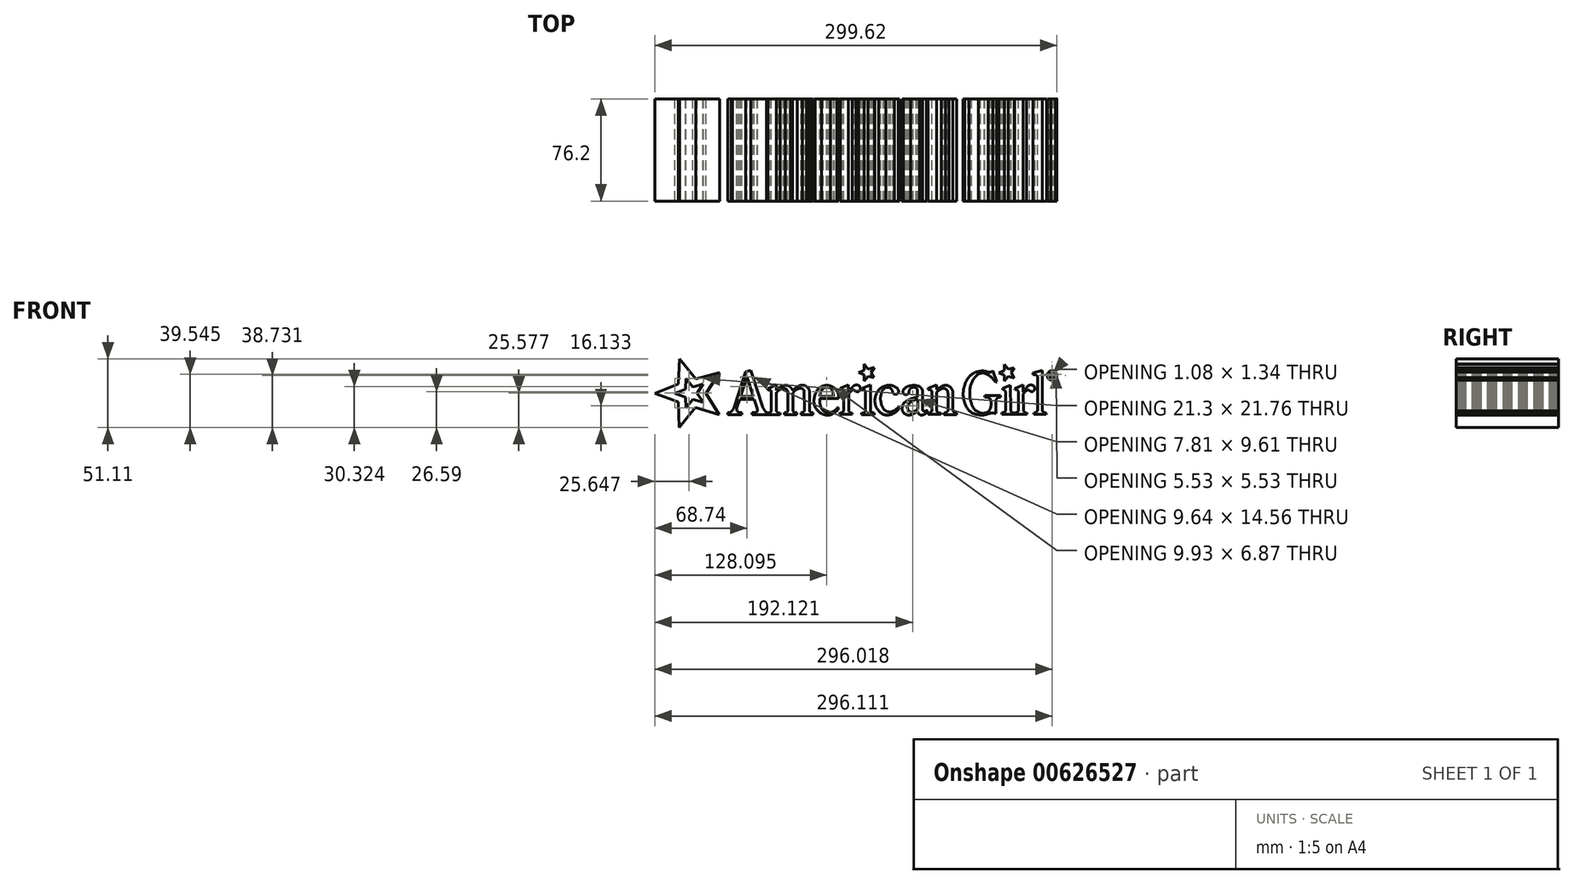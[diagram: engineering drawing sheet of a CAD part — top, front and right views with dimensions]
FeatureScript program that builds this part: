
annotation { "Feature Type Name" : "Feature", "Feature Type Description" : "" }
export const myFeature = defineFeature(function(context is Context, id is Id, definition is map)
    precondition{}
    {
        {
            var Q0;
            Q0=qCreatedBy(makeId("Front.planeOp"),FACE);
            var sketch = newSketch(context, id + "F0", { "sketchPlane" : qUnion([Q0])});
            skLineSegment(sketch, "E0", {"start": v(-64.16, 36.86) * mm, "end": v(-72.1, 33.85) * mm});
            skLineSegment(sketch, "E1", {"start": v(-72.1, 33.85) * mm, "end": v(-64.16, 31.03) * mm});
            skLineSegment(sketch, "E2", {"start": v(-64.16, 31.03) * mm, "end": v(-63.64, 23.1) * mm});
            skLineSegment(sketch, "E3", {"start": v(-63.64, 23.1) * mm, "end": v(-58.72, 29.32) * mm});
            skLineSegment(sketch, "E4", {"start": v(-58.72, 29.32) * mm, "end": v(-50.8, 26.96) * mm});
            skLineSegment(sketch, "E5", {"start": v(-50.8, 26.96) * mm, "end": v(-55.38, 33.85) * mm});
            skLineSegment(sketch, "E6", {"start": v(-55.38, 33.85) * mm, "end": v(-50.92, 40.6) * mm});
            skLineSegment(sketch, "E7", {"start": v(-50.92, 40.6) * mm, "end": v(-58.6, 38.5) * mm});
            skLineSegment(sketch, "E8", {"start": v(-58.6, 38.5) * mm, "end": v(-63.64, 44.86) * mm});
            skLineSegment(sketch, "E9", {"start": v(-63.64, 44.86) * mm, "end": v(-64.16, 36.86) * mm});
            skLineSegment(sketch, "E10", {"start": v(-69.43, 40.6) * mm, "end": v(-87.1, 33.85) * mm});
            skPoint(sketch, "E10.endSnap0", {"position": v(-87.1, 33.95) * mm});
            skLineSegment(sketch, "E11", {"start": v(-87.1, 33.85) * mm, "end": v(-69.33, 27.53) * mm});
            skLineSegment(sketch, "E12", {"start": v(-69.33, 27.53) * mm, "end": v(-68.79, 8.4) * mm});
            skLineSegment(sketch, "E13", {"start": v(-68.79, 8.4) * mm, "end": v(-56.93, 23.25) * mm});
            skLineSegment(sketch, "E14", {"start": v(-56.93, 23.25) * mm, "end": v(-38.87, 17.96) * mm});
            skLineSegment(sketch, "E15", {"start": v(-38.87, 17.96) * mm, "end": v(-48.84, 33.79) * mm});
            skLineSegment(sketch, "E16", {"start": v(-48.84, 33.79) * mm, "end": v(-38.56, 49.4) * mm});
            skLineSegment(sketch, "E17", {"start": v(-38.56, 49.4) * mm, "end": v(-56.57, 44.63) * mm});
            skLineSegment(sketch, "E18", {"start": v(-56.57, 44.63) * mm, "end": v(-68.38, 59.5) * mm});
            skLineSegment(sketch, "E19", {"start": v(-68.38, 59.5) * mm, "end": v(-69.43, 40.6) * mm});
            skLineSegment(sketch, "E20", {"start": v(-23.17, 31.44) * mm, "end": v(-13.53, 31.44) * mm});
            skLineSegment(sketch, "E21", {"start": v(-13.53, 31.44) * mm, "end": v(-18.27, 46) * mm});
            skLineSegment(sketch, "E22", {"start": v(-18.27, 46) * mm, "end": v(-23.17, 31.44) * mm});
            skLineSegment(sketch, "E23", {"start": v(-19.42, 49.88) * mm, "end": v(-15.52, 50.95) * mm});
            skLineSegment(sketch, "E24", {"start": v(-23.84, 29.47) * mm, "end": v(-13.1, 29.47) * mm});
            skLineSegment(sketch, "E25", {"start": v(-15.52, 50.95) * mm, "end": v(-6.5, 23.57) * mm});
            skLineSegment(sketch, "E26", {"start": v(-19.42, 49.88) * mm, "end": v(-28.04, 23.24) * mm});
            skLineSegment(sketch, "E27", {"start": v(-23.84, 29.47) * mm, "end": v(-25.84, 22.87) * mm});
            skLineSegment(sketch, "E28", {"start": v(-13.1, 29.47) * mm, "end": v(-10.8, 22.62) * mm});
            skLineSegment(sketch, "E29", {"start": v(-32.76, 19.4) * mm, "end": v(-32.76, 18.03) * mm});
            skLineSegment(sketch, "E30", {"start": v(-32.76, 18.03) * mm, "end": v(-22.12, 18.03) * mm});
            skLineSegment(sketch, "E31", {"start": v(-22.12, 18.03) * mm, "end": v(-22.12, 19.34) * mm});
            skLineSegment(sketch, "E32", {"start": v(-22.12, 19.34) * mm, "end": v(-23.42, 19.34) * mm});
            skLineSegment(sketch, "E33", {"start": v(-32.76, 19.4) * mm, "end": v(-31.77, 19.4) * mm});
            skLineSegment(sketch, "E34", {"start": v(-14.62, 19.43) * mm, "end": v(-14.62, 18) * mm});
            skLineSegment(sketch, "E35", {"start": v(-14.62, 18) * mm, "end": v(6.53, 18) * mm});
            skLineSegment(sketch, "E36", {"start": v(6.53, 18) * mm, "end": v(6.53, 19.13) * mm});
            skLineSegment(sketch, "E37", {"start": v(6.53, 19.13) * mm, "end": v(5.77, 19.13) * mm});
            skLineSegment(sketch, "E38", {"start": v(-14.62, 19.43) * mm, "end": v(-12.2, 19.43) * mm});
            skArc(sketch, "E39", {"start": v(-12.2, 19.43) * mm, "mid": v(-11.19, 19.79) * mm, "end": v(-10.62, 20.7) * mm});
            skArc(sketch, "E40", {"start": v(-10.62, 20.7) * mm, "mid": v(-10.56, 21.23) * mm, "end": v(-10.62, 21.77) * mm});
            skArc(sketch, "E41", {"start": v(-10.62, 21.77) * mm, "mid": v(-10.7, 22.2) * mm, "end": v(-10.8, 22.62) * mm});
            skArc(sketch, "E42", {"start": v(-24.65, 19.83) * mm, "mid": v(-24.08, 19.47) * mm, "end": v(-23.42, 19.34) * mm});
            skArc(sketch, "E43", {"start": v(-25.68, 20.8) * mm, "mid": v(-25.28, 20.2) * mm, "end": v(-24.65, 19.83) * mm});
            skArc(sketch, "E44", {"start": v(-25.84, 22.87) * mm, "mid": v(-25.95, 21.82) * mm, "end": v(-25.68, 20.8) * mm});
            skArc(sketch, "E45", {"start": v(-31.77, 19.4) * mm, "mid": v(-30.94, 19.57) * mm, "end": v(-30.27, 20.09) * mm});
            skArc(sketch, "E46", {"start": v(-30.27, 20.09) * mm, "mid": v(-29.58, 20.62) * mm, "end": v(-29.03, 21.3) * mm});
            skArc(sketch, "E47", {"start": v(-29.03, 21.3) * mm, "mid": v(-28.45, 22.23) * mm, "end": v(-28.04, 23.24) * mm});
            skArc(sketch, "E48", {"start": v(-6.5, 23.57) * mm, "mid": v(-5.45, 21.42) * mm, "end": v(-3.88, 19.62) * mm});
            skArc(sketch, "E49", {"start": v(-3.88, 19.62) * mm, "mid": v(-2.4, 19.27) * mm, "end": v(-0.93, 19.62) * mm});
            skArc(sketch, "E50", {"start": v(-0.93, 19.62) * mm, "mid": v(-0.43, 20.28) * mm, "end": v(-0.25, 21.07) * mm});
            skLineSegment(sketch, "E51", {"start": v(-0.25, 21.07) * mm, "end": v(-0.25, 34.6) * mm});
            skArc(sketch, "E52", {"start": v(-0.25, 34.6) * mm, "mid": v(-0.32, 35.18) * mm, "end": v(-0.5, 35.73) * mm});
            skArc(sketch, "E53", {"start": v(-0.5, 35.73) * mm, "mid": v(-0.88, 36.15) * mm, "end": v(-1.41, 36.3) * mm});
            skArc(sketch, "E54", {"start": v(-1.41, 36.3) * mm, "mid": v(-2.1, 36.39) * mm, "end": v(-2.78, 36.3) * mm});
            skLineSegment(sketch, "E55", {"start": v(-2.78, 36.3) * mm, "end": v(-2.78, 37.36) * mm});
            skLineSegment(sketch, "E56", {"start": v(-2.78, 37.36) * mm, "end": v(3.53, 40.06) * mm});
            skLineSegment(sketch, "E57", {"start": v(3.53, 40.06) * mm, "end": v(3.53, 35.88) * mm});
            skArc(sketch, "E58", {"start": v(3.78, 20.36) * mm, "mid": v(4.6, 19.46) * mm, "end": v(5.77, 19.13) * mm});
            skArc(sketch, "E59", {"start": v(3.57, 21.04) * mm, "mid": v(3.63, 20.68) * mm, "end": v(3.78, 20.36) * mm});
            skLineSegment(sketch, "E60", {"start": v(3.57, 21.04) * mm, "end": v(3.57, 34.16) * mm});
            skArc(sketch, "E61", {"start": v(4.9, 35.53) * mm, "mid": v(4.18, 34.9) * mm, "end": v(3.57, 34.16) * mm});
            skArc(sketch, "E62", {"start": v(8.49, 37.37) * mm, "mid": v(6.53, 36.77) * mm, "end": v(4.9, 35.53) * mm});
            skArc(sketch, "E63", {"start": v(10.72, 37.05) * mm, "mid": v(9.63, 37.39) * mm, "end": v(8.49, 37.37) * mm});
            skArc(sketch, "E64", {"start": v(12.05, 34.48) * mm, "mid": v(11.7, 35.93) * mm, "end": v(10.72, 37.05) * mm});
            skLineSegment(sketch, "E65", {"start": v(12.05, 34.48) * mm, "end": v(12.05, 21.12) * mm});
            skArc(sketch, "E66", {"start": v(11.67, 19.95) * mm, "mid": v(11.95, 20.5) * mm, "end": v(12.05, 21.12) * mm});
            skArc(sketch, "E67", {"start": v(9.45, 19.36) * mm, "mid": v(10.61, 19.44) * mm, "end": v(11.67, 19.95) * mm});
            skLineSegment(sketch, "E68", {"start": v(9.45, 19.36) * mm, "end": v(9.45, 17.88) * mm});
            skLineSegment(sketch, "E69", {"start": v(9.45, 17.88) * mm, "end": v(18.73, 17.88) * mm});
            skLineSegment(sketch, "E70", {"start": v(18.73, 17.88) * mm, "end": v(18.73, 19.36) * mm});
            skLineSegment(sketch, "E71", {"start": v(15.84, 34.27) * mm, "end": v(15.84, 21.13) * mm});
            skArc(sketch, "E72", {"start": v(15.84, 21.13) * mm, "mid": v(16.92, 19.65) * mm, "end": v(18.73, 19.36) * mm});
            skArc(sketch, "E73", {"start": v(19.18, 36.87) * mm, "mid": v(17.39, 35.72) * mm, "end": v(15.84, 34.27) * mm});
            skArc(sketch, "E74", {"start": v(22.82, 37.28) * mm, "mid": v(20.96, 37.47) * mm, "end": v(19.18, 36.87) * mm});
            skArc(sketch, "E75", {"start": v(24.33, 34.88) * mm, "mid": v(23.94, 36.3) * mm, "end": v(22.82, 37.28) * mm});
            skLineSegment(sketch, "E76", {"start": v(24.33, 34.88) * mm, "end": v(24.48, 21.7) * mm});
            skArc(sketch, "E77", {"start": v(23.86, 19.84) * mm, "mid": v(24.33, 20.72) * mm, "end": v(24.48, 21.7) * mm});
            skArc(sketch, "E78", {"start": v(21.8, 19.34) * mm, "mid": v(22.86, 19.46) * mm, "end": v(23.86, 19.84) * mm});
            skLineSegment(sketch, "E79", {"start": v(21.8, 19.34) * mm, "end": v(21.8, 17.93) * mm});
            skLineSegment(sketch, "E80", {"start": v(21.8, 17.93) * mm, "end": v(31, 17.93) * mm});
            skLineSegment(sketch, "E81", {"start": v(31, 17.93) * mm, "end": v(31, 19.34) * mm});
            skArc(sketch, "E82", {"start": v(28.79, 19.88) * mm, "mid": v(29.85, 19.44) * mm, "end": v(31, 19.34) * mm});
            skArc(sketch, "E83", {"start": v(28.39, 20.94) * mm, "mid": v(28.46, 20.36) * mm, "end": v(28.79, 19.88) * mm});
            skLineSegment(sketch, "E84", {"start": v(28.39, 20.94) * mm, "end": v(28.39, 34.4) * mm});
            skArc(sketch, "E85", {"start": v(28.39, 34.4) * mm, "mid": v(27.77, 36.88) * mm, "end": v(26.06, 38.78) * mm});
            skArc(sketch, "E86", {"start": v(26.06, 38.78) * mm, "mid": v(24.61, 39.6) * mm, "end": v(22.94, 39.68) * mm});
            skArc(sketch, "E87", {"start": v(22.94, 39.68) * mm, "mid": v(20.9, 39.5) * mm, "end": v(19.09, 38.6) * mm});
            skArc(sketch, "E88", {"start": v(19.09, 38.6) * mm, "mid": v(17.27, 37.37) * mm, "end": v(15.68, 35.85) * mm});
            skArc(sketch, "E89", {"start": v(15.68, 35.85) * mm, "mid": v(15.03, 37.25) * mm, "end": v(13.96, 38.37) * mm});
            skArc(sketch, "E90", {"start": v(13.96, 38.37) * mm, "mid": v(12.23, 39.53) * mm, "end": v(10.15, 39.68) * mm});
            skArc(sketch, "E91", {"start": v(10.15, 39.68) * mm, "mid": v(8.17, 39.37) * mm, "end": v(6.42, 38.37) * mm});
            skArc(sketch, "E92", {"start": v(6.42, 38.37) * mm, "mid": v(4.8, 37.34) * mm, "end": v(3.53, 35.88) * mm});
            skLineSegment(sketch, "E93", {"start": v(36.04, 31.56) * mm, "end": v(45.96, 31.56) * mm});
            skLineSegment(sketch, "E94", {"start": v(35.91, 29.9) * mm, "end": v(49.99, 29.9) * mm});
            skLineSegment(sketch, "E95", {"start": v(35.91, 29.9) * mm, "end": v(35.91, 27.94) * mm});
            skArc(sketch, "E96", {"start": v(35.91, 27.94) * mm, "mid": v(36.2, 25.43) * mm, "end": v(37.03, 23.05) * mm});
            skArc(sketch, "E97", {"start": v(37.03, 23.05) * mm, "mid": v(38.53, 20.82) * mm, "end": v(40.9, 19.56) * mm});
            skArc(sketch, "E98", {"start": v(40.9, 19.56) * mm, "mid": v(43.88, 19.58) * mm, "end": v(46.63, 20.74) * mm});
            skArc(sketch, "E99", {"start": v(46.63, 20.74) * mm, "mid": v(48.02, 21.94) * mm, "end": v(49.22, 23.33) * mm});
            skLineSegment(sketch, "E100", {"start": v(49.22, 23.33) * mm, "end": v(50.02, 22.7) * mm});
            skArc(sketch, "E101", {"start": v(43.85, 17.77) * mm, "mid": v(47.36, 19.7) * mm, "end": v(50.02, 22.7) * mm});
            skArc(sketch, "E102", {"start": v(37.35, 18.53) * mm, "mid": v(40.53, 17.6) * mm, "end": v(43.85, 17.77) * mm});
            skArc(sketch, "E103", {"start": v(31.78, 25.83) * mm, "mid": v(33.8, 21.6) * mm, "end": v(37.35, 18.53) * mm});
            skArc(sketch, "E104", {"start": v(32.55, 33.16) * mm, "mid": v(31.66, 29.55) * mm, "end": v(31.78, 25.83) * mm});
            skArc(sketch, "E105", {"start": v(37.35, 38.92) * mm, "mid": v(34.39, 36.5) * mm, "end": v(32.55, 33.16) * mm});
            skArc(sketch, "E106", {"start": v(43.85, 39.43) * mm, "mid": v(40.56, 39.72) * mm, "end": v(37.35, 38.92) * mm});
            skArc(sketch, "E107", {"start": v(48.55, 35.68) * mm, "mid": v(46.52, 37.96) * mm, "end": v(43.85, 39.43) * mm});
            skArc(sketch, "E108", {"start": v(49.99, 29.9) * mm, "mid": v(49.78, 32.91) * mm, "end": v(48.55, 35.68) * mm});
            skArc(sketch, "E109", {"start": v(38.34, 37.32) * mm, "mid": v(36.57, 34.68) * mm, "end": v(36.04, 31.56) * mm});
            skArc(sketch, "E110", {"start": v(42.37, 38.28) * mm, "mid": v(40.24, 38.3) * mm, "end": v(38.34, 37.32) * mm});
            skArc(sketch, "E111", {"start": v(45.64, 34.88) * mm, "mid": v(44.46, 37.02) * mm, "end": v(42.37, 38.28) * mm});
            skArc(sketch, "E112", {"start": v(45.96, 31.56) * mm, "mid": v(45.92, 33.23) * mm, "end": v(45.64, 34.88) * mm});
            skLineSegment(sketch, "E113", {"start": v(51.04, 37.46) * mm, "end": v(51.04, 36.47) * mm});
            skLineSegment(sketch, "E114", {"start": v(51.04, 37.46) * mm, "end": v(57.31, 39.97) * mm});
            skArc(sketch, "E115", {"start": v(53.19, 35.68) * mm, "mid": v(52.24, 36.42) * mm, "end": v(51.04, 36.47) * mm});
            skArc(sketch, "E116", {"start": v(53.6, 34.16) * mm, "mid": v(53.5, 34.95) * mm, "end": v(53.19, 35.68) * mm});
            skLineSegment(sketch, "E117", {"start": v(53.6, 34.16) * mm, "end": v(53.6, 21.33) * mm});
            skLineSegment(sketch, "E118", {"start": v(50.88, 19.31) * mm, "end": v(50.88, 18.08) * mm});
            skLineSegment(sketch, "E119", {"start": v(50.88, 18.08) * mm, "end": v(60.16, 18.08) * mm});
            skLineSegment(sketch, "E120", {"start": v(60.16, 18.08) * mm, "end": v(60.16, 19.19) * mm});
            skArc(sketch, "E121", {"start": v(50.88, 19.31) * mm, "mid": v(52.75, 19.64) * mm, "end": v(53.6, 21.33) * mm});
            skArc(sketch, "E122", {"start": v(57.4, 21.33) * mm, "mid": v(58.29, 19.63) * mm, "end": v(60.16, 19.19) * mm});
            skLineSegment(sketch, "E123", {"start": v(57.4, 21.33) * mm, "end": v(57.4, 33.02) * mm});
            skLineSegment(sketch, "E124", {"start": v(57.31, 39.97) * mm, "end": v(57.31, 34.96) * mm});
            skArc(sketch, "E125", {"start": v(60.09, 38.28) * mm, "mid": v(58.66, 36.66) * mm, "end": v(57.31, 34.96) * mm});
            skArc(sketch, "E126", {"start": v(62.84, 39.95) * mm, "mid": v(61.25, 39.47) * mm, "end": v(60.09, 38.28) * mm});
            skArc(sketch, "E127", {"start": v(65.65, 38.9) * mm, "mid": v(64.43, 39.9) * mm, "end": v(62.84, 39.95) * mm});
            skArc(sketch, "E128", {"start": v(65.87, 36.36) * mm, "mid": v(66.1, 37.66) * mm, "end": v(65.65, 38.9) * mm});
            skArc(sketch, "E129", {"start": v(63.9, 34.96) * mm, "mid": v(65.08, 35.4) * mm, "end": v(65.87, 36.36) * mm});
            skArc(sketch, "E130", {"start": v(61.79, 36.14) * mm, "mid": v(62.72, 35.32) * mm, "end": v(63.9, 34.96) * mm});
            skArc(sketch, "E131", {"start": v(61.79, 36.14) * mm, "mid": v(60.94, 36.32) * mm, "end": v(60.09, 36.14) * mm});
            skArc(sketch, "E132", {"start": v(60.09, 36.14) * mm, "mid": v(58.52, 34.78) * mm, "end": v(57.4, 33.02) * mm});
            skLineSegment(sketch, "E133", {"start": v(67.62, 37.5) * mm, "end": v(67.62, 36.39) * mm});
            skLineSegment(sketch, "E134", {"start": v(67.62, 37.5) * mm, "end": v(73.59, 40.08) * mm});
            skLineSegment(sketch, "E135", {"start": v(73.59, 40.08) * mm, "end": v(73.59, 20.97) * mm});
            skLineSegment(sketch, "E136", {"start": v(69.03, 55.54) * mm, "end": v(69.03, 50.83) * mm});
            skLineSegment(sketch, "E137", {"start": v(69.03, 50.83) * mm, "end": v(64.67, 49.31) * mm});
            skLineSegment(sketch, "E138", {"start": v(64.67, 49.31) * mm, "end": v(68.85, 47.62) * mm});
            skLineSegment(sketch, "E139", {"start": v(68.85, 47.62) * mm, "end": v(68.85, 42.97) * mm});
            skLineSegment(sketch, "E140", {"start": v(68.85, 42.97) * mm, "end": v(71.84, 46.5) * mm});
            skLineSegment(sketch, "E141", {"start": v(71.84, 46.5) * mm, "end": v(76.23, 45.35) * mm});
            skLineSegment(sketch, "E142", {"start": v(76.23, 45.35) * mm, "end": v(73.9, 49.11) * mm});
            skLineSegment(sketch, "E143", {"start": v(73.9, 49.11) * mm, "end": v(76.48, 53.1) * mm});
            skLineSegment(sketch, "E144", {"start": v(76.48, 53.1) * mm, "end": v(71.92, 51.8) * mm});
            skLineSegment(sketch, "E145", {"start": v(71.92, 51.8) * mm, "end": v(69.03, 55.54) * mm});
            skArc(sketch, "E146", {"start": v(69.24, 36.17) * mm, "mid": v(68.45, 36.43) * mm, "end": v(67.62, 36.39) * mm});
            skArc(sketch, "E147", {"start": v(69.93, 35.33) * mm, "mid": v(69.67, 35.82) * mm, "end": v(69.24, 36.17) * mm});
            skLineSegment(sketch, "E148", {"start": v(69.93, 35.33) * mm, "end": v(69.93, 21.32) * mm});
            skArc(sketch, "E149", {"start": v(73.59, 20.97) * mm, "mid": v(74.14, 19.75) * mm, "end": v(75.42, 19.35) * mm});
            skLineSegment(sketch, "E150", {"start": v(76.52, 19.22) * mm, "end": v(76.52, 17.99) * mm});
            skLineSegment(sketch, "E151", {"start": v(76.52, 17.99) * mm, "end": v(67.16, 17.99) * mm});
            skLineSegment(sketch, "E152", {"start": v(67.16, 17.99) * mm, "end": v(67.16, 19.32) * mm});
            skArc(sketch, "E153", {"start": v(67.16, 19.32) * mm, "mid": v(69.05, 19.61) * mm, "end": v(69.93, 21.32) * mm});
            skArc(sketch, "E154", {"start": v(75.42, 19.35) * mm, "mid": v(75.96, 19.22) * mm, "end": v(76.52, 19.22) * mm});
            skArc(sketch, "E155", {"start": v(84.02, 37.55) * mm, "mid": v(82.23, 35.21) * mm, "end": v(81.45, 32.37) * mm});
            skArc(sketch, "E156", {"start": v(81.45, 32.37) * mm, "mid": v(81.13, 29.83) * mm, "end": v(81.45, 27.29) * mm});
            skArc(sketch, "E157", {"start": v(81.45, 27.29) * mm, "mid": v(82.12, 24.7) * mm, "end": v(83.29, 22.3) * mm});
            skArc(sketch, "E158", {"start": v(83.29, 22.3) * mm, "mid": v(85.31, 20.57) * mm, "end": v(87.87, 19.86) * mm});
            skArc(sketch, "E159", {"start": v(87.87, 19.86) * mm, "mid": v(91.65, 21.03) * mm, "end": v(94.56, 23.71) * mm});
            skArc(sketch, "E160", {"start": v(88.7, 37.55) * mm, "mid": v(86.36, 38.35) * mm, "end": v(84.02, 37.55) * mm});
            skArc(sketch, "E161", {"start": v(90.12, 34.85) * mm, "mid": v(89.62, 36.31) * mm, "end": v(88.7, 37.55) * mm});
            skArc(sketch, "E162", {"start": v(90.12, 34.85) * mm, "mid": v(91.56, 33.17) * mm, "end": v(93.74, 33.56) * mm});
            skArc(sketch, "E163", {"start": v(93.74, 33.56) * mm, "mid": v(94.57, 35.03) * mm, "end": v(94.2, 36.68) * mm});
            skArc(sketch, "E164", {"start": v(94.2, 36.68) * mm, "mid": v(93.09, 38.01) * mm, "end": v(91.54, 38.79) * mm});
            skArc(sketch, "E165", {"start": v(91.54, 38.79) * mm, "mid": v(88.35, 39.86) * mm, "end": v(85.01, 39.37) * mm});
            skArc(sketch, "E166", {"start": v(85.01, 39.37) * mm, "mid": v(81.97, 38.17) * mm, "end": v(79.6, 35.9) * mm});
            skArc(sketch, "E167", {"start": v(79.6, 35.9) * mm, "mid": v(77.54, 32.28) * mm, "end": v(77.04, 28.15) * mm});
            skArc(sketch, "E168", {"start": v(77.04, 28.15) * mm, "mid": v(77.56, 24.28) * mm, "end": v(79.6, 20.95) * mm});
            skArc(sketch, "E169", {"start": v(79.6, 20.95) * mm, "mid": v(83, 18.2) * mm, "end": v(87.35, 17.65) * mm});
            skArc(sketch, "E170", {"start": v(87.35, 17.65) * mm, "mid": v(91.01, 18.87) * mm, "end": v(94, 21.32) * mm});
            skArc(sketch, "E171", {"start": v(94, 21.32) * mm, "mid": v(94.62, 22.21) * mm, "end": v(95.23, 23.1) * mm});
            skLineSegment(sketch, "E172", {"start": v(94.56, 23.71) * mm, "end": v(95.23, 23.1) * mm});
            skArc(sketch, "E173", {"start": v(100.55, 32.82) * mm, "mid": v(101.83, 33.67) * mm, "end": v(102.38, 35.11) * mm});
            skArc(sketch, "E174", {"start": v(98.26, 33.6) * mm, "mid": v(99.31, 32.95) * mm, "end": v(100.55, 32.82) * mm});
            skArc(sketch, "E175", {"start": v(98.26, 36.49) * mm, "mid": v(97.9, 35.04) * mm, "end": v(98.26, 33.6) * mm});
            skArc(sketch, "E176", {"start": v(103.53, 39.42) * mm, "mid": v(100.55, 38.57) * mm, "end": v(98.26, 36.49) * mm});
            skArc(sketch, "E177", {"start": v(110.13, 38.82) * mm, "mid": v(106.88, 39.72) * mm, "end": v(103.53, 39.42) * mm});
            skArc(sketch, "E178", {"start": v(112.42, 35.94) * mm, "mid": v(111.58, 37.63) * mm, "end": v(110.13, 38.82) * mm});
            skArc(sketch, "E179", {"start": v(104.81, 38.18) * mm, "mid": v(103.12, 37.02) * mm, "end": v(102.38, 35.11) * mm});
            skArc(sketch, "E180", {"start": v(107.7, 37.77) * mm, "mid": v(106.3, 38.35) * mm, "end": v(104.81, 38.18) * mm});
            skArc(sketch, "E181", {"start": v(108.75, 35.11) * mm, "mid": v(108.52, 36.56) * mm, "end": v(107.7, 37.77) * mm});
            skLineSegment(sketch, "E182", {"start": v(108.75, 35.11) * mm, "end": v(108.75, 30.99) * mm});
            skLineSegment(sketch, "E183", {"start": v(112.42, 35.94) * mm, "end": v(112.42, 21.91) * mm});
            skLineSegment(sketch, "E184", {"start": v(108.94, 29.34) * mm, "end": v(108.94, 22.46) * mm});
            skLineSegment(sketch, "E185", {"start": v(115.4, 21.46) * mm, "end": v(116, 20.58) * mm});
            skArc(sketch, "E186", {"start": v(112.42, 21.91) * mm, "mid": v(113.71, 20.4) * mm, "end": v(115.4, 21.46) * mm});
            skArc(sketch, "E187", {"start": v(108.94, 29.34) * mm, "mid": v(104.69, 28.11) * mm, "end": v(101.56, 24.98) * mm});
            skArc(sketch, "E188", {"start": v(101.56, 24.98) * mm, "mid": v(101.12, 23.45) * mm, "end": v(101.56, 21.91) * mm});
            skArc(sketch, "E189", {"start": v(101.56, 21.91) * mm, "mid": v(103.07, 20.06) * mm, "end": v(105.45, 19.9) * mm});
            skArc(sketch, "E190", {"start": v(105.45, 19.9) * mm, "mid": v(107.33, 21) * mm, "end": v(108.94, 22.46) * mm});
            skArc(sketch, "E191", {"start": v(108.75, 30.99) * mm, "mid": v(104.14, 29.84) * mm, "end": v(99.95, 27.6) * mm});
            skArc(sketch, "E192", {"start": v(99.95, 27.6) * mm, "mid": v(98.08, 25.76) * mm, "end": v(97.34, 23.24) * mm});
            skArc(sketch, "E193", {"start": v(97.34, 23.24) * mm, "mid": v(97.38, 20.97) * mm, "end": v(98.63, 19.07) * mm});
            skArc(sketch, "E194", {"start": v(98.63, 19.07) * mm, "mid": v(101.67, 17.6) * mm, "end": v(105, 18.2) * mm});
            skArc(sketch, "E195", {"start": v(105, 18.2) * mm, "mid": v(106.96, 19.2) * mm, "end": v(108.75, 20.5) * mm});
            skArc(sketch, "E196", {"start": v(108.75, 20.5) * mm, "mid": v(109.54, 18.7) * mm, "end": v(111.18, 17.6) * mm});
            skArc(sketch, "E197", {"start": v(111.18, 17.6) * mm, "mid": v(114.09, 18.29) * mm, "end": v(116, 20.58) * mm});
            skLineSegment(sketch, "E198", {"start": v(116.6, 37.59) * mm, "end": v(116.6, 36.58) * mm});
            skLineSegment(sketch, "E199", {"start": v(116.6, 37.59) * mm, "end": v(122.96, 40.06) * mm});
            skLineSegment(sketch, "E200", {"start": v(122.96, 40.06) * mm, "end": v(122.96, 36.49) * mm});
            skLineSegment(sketch, "E201", {"start": v(116.5, 19.26) * mm, "end": v(116.5, 18.06) * mm});
            skLineSegment(sketch, "E202", {"start": v(116.5, 18.06) * mm, "end": v(125.99, 18.06) * mm});
            skLineSegment(sketch, "E203", {"start": v(125.99, 18.06) * mm, "end": v(125.99, 19.16) * mm});
            skLineSegment(sketch, "E204", {"start": v(123.05, 34.7) * mm, "end": v(123.05, 21.27) * mm});
            skLineSegment(sketch, "E205", {"start": v(128.46, 19.26) * mm, "end": v(128.46, 17.97) * mm});
            skLineSegment(sketch, "E206", {"start": v(128.46, 17.97) * mm, "end": v(137.95, 17.97) * mm});
            skLineSegment(sketch, "E207", {"start": v(137.95, 17.97) * mm, "end": v(137.95, 19.26) * mm});
            skLineSegment(sketch, "E208", {"start": v(131.35, 20.9) * mm, "end": v(131.35, 34.2) * mm});
            skLineSegment(sketch, "E209", {"start": v(135.1, 21) * mm, "end": v(135.1, 34.01) * mm});
            skArc(sketch, "E210", {"start": v(127.73, 37.5) * mm, "mid": v(125.2, 36.43) * mm, "end": v(123.05, 34.7) * mm});
            skArc(sketch, "E211", {"start": v(131.35, 34.2) * mm, "mid": v(130.27, 36.65) * mm, "end": v(127.73, 37.5) * mm});
            skArc(sketch, "E212", {"start": v(123.05, 21.27) * mm, "mid": v(123.98, 19.47) * mm, "end": v(125.99, 19.16) * mm});
            skArc(sketch, "E213", {"start": v(128.46, 19.26) * mm, "mid": v(130.15, 19.65) * mm, "end": v(131.35, 20.9) * mm});
            skArc(sketch, "E214", {"start": v(135.1, 21) * mm, "mid": v(136.25, 19.68) * mm, "end": v(137.95, 19.26) * mm});
            skArc(sketch, "E215", {"start": v(135.1, 34.01) * mm, "mid": v(134.3, 36.98) * mm, "end": v(132.13, 39.15) * mm});
            skArc(sketch, "E216", {"start": v(126.3, 38.73) * mm, "mid": v(124.58, 37.7) * mm, "end": v(122.96, 36.49) * mm});
            skArc(sketch, "E217", {"start": v(129.51, 39.79) * mm, "mid": v(127.82, 39.54) * mm, "end": v(126.3, 38.73) * mm});
            skArc(sketch, "E218", {"start": v(132.13, 39.15) * mm, "mid": v(130.88, 39.7) * mm, "end": v(129.51, 39.79) * mm});
            skLineSegment(sketch, "E219", {"start": v(119.34, 34.75) * mm, "end": v(119.34, 21.27) * mm});
            skArc(sketch, "E220", {"start": v(119.34, 34.75) * mm, "mid": v(118.46, 36.4) * mm, "end": v(116.6, 36.58) * mm});
            skArc(sketch, "E221", {"start": v(116.5, 19.26) * mm, "mid": v(118.44, 19.53) * mm, "end": v(119.34, 21.27) * mm});
            skLineSegment(sketch, "E222", {"start": v(158.77, 30.83) * mm, "end": v(158.77, 32.14) * mm});
            skLineSegment(sketch, "E223", {"start": v(158.77, 32.14) * mm, "end": v(170.6, 32.14) * mm});
            skLineSegment(sketch, "E224", {"start": v(170.6, 32.14) * mm, "end": v(170.6, 30.83) * mm});
            skLineSegment(sketch, "E225", {"start": v(164.99, 50.5) * mm, "end": v(167.82, 42.44) * mm});
            skLineSegment(sketch, "E226", {"start": v(167.82, 42.44) * mm, "end": v(166.73, 42.05) * mm});
            skLineSegment(sketch, "E227", {"start": v(167.11, 18.73) * mm, "end": v(167.11, 28.05) * mm});
            skArc(sketch, "E228", {"start": v(170.6, 30.83) * mm, "mid": v(168.19, 30.28) * mm, "end": v(167.11, 28.05) * mm});
            skArc(sketch, "E229", {"start": v(161.39, 49.52) * mm, "mid": v(163.27, 49.7) * mm, "end": v(164.99, 50.5) * mm});
            skArc(sketch, "E230", {"start": v(162.8, 29.8) * mm, "mid": v(160.92, 30.83) * mm, "end": v(158.77, 30.83) * mm});
            skArc(sketch, "E231", {"start": v(163.46, 25.27) * mm, "mid": v(163.38, 27.57) * mm, "end": v(162.8, 29.8) * mm});
            skArc(sketch, "E232", {"start": v(161.28, 20.04) * mm, "mid": v(162.9, 22.43) * mm, "end": v(163.46, 25.27) * mm});
            skArc(sketch, "E233", {"start": v(153.7, 20.04) * mm, "mid": v(157.5, 18.91) * mm, "end": v(161.28, 20.04) * mm});
            skArc(sketch, "E234", {"start": v(148.8, 26.3) * mm, "mid": v(150.52, 22.6) * mm, "end": v(153.7, 20.04) * mm});
            skArc(sketch, "E235", {"start": v(147.82, 37.37) * mm, "mid": v(147.63, 31.78) * mm, "end": v(148.8, 26.3) * mm});
            skArc(sketch, "E236", {"start": v(154.41, 48.38) * mm, "mid": v(149.91, 43.6) * mm, "end": v(147.82, 37.37) * mm});
            skArc(sketch, "E237", {"start": v(158.6, 48.81) * mm, "mid": v(156.48, 48.89) * mm, "end": v(154.41, 48.38) * mm});
            skArc(sketch, "E238", {"start": v(166.73, 42.05) * mm, "mid": v(163.29, 46.18) * mm, "end": v(158.6, 48.81) * mm});
            skArc(sketch, "E239", {"start": v(167.11, 18.73) * mm, "mid": v(164.52, 19.13) * mm, "end": v(161.93, 18.73) * mm});
            skArc(sketch, "E240", {"start": v(161.39, 49.52) * mm, "mid": v(157.73, 50.42) * mm, "end": v(153.98, 50.07) * mm});
            skArc(sketch, "E241", {"start": v(153.98, 50.07) * mm, "mid": v(150.16, 48.63) * mm, "end": v(147.1, 45.93) * mm});
            skArc(sketch, "E242", {"start": v(147.1, 45.93) * mm, "mid": v(145.07, 43.09) * mm, "end": v(143.84, 39.82) * mm});
            skArc(sketch, "E243", {"start": v(143.84, 39.82) * mm, "mid": v(142.79, 35.05) * mm, "end": v(142.97, 30.17) * mm});
            skArc(sketch, "E244", {"start": v(142.97, 30.17) * mm, "mid": v(144.18, 25.76) * mm, "end": v(146.46, 21.78) * mm});
            skArc(sketch, "E245", {"start": v(146.46, 21.78) * mm, "mid": v(150.56, 18.67) * mm, "end": v(155.61, 17.7) * mm});
            skArc(sketch, "E246", {"start": v(155.61, 17.7) * mm, "mid": v(158.84, 17.8) * mm, "end": v(161.93, 18.73) * mm});
            skLineSegment(sketch, "E247", {"start": v(173.32, 51) * mm, "end": v(173.32, 55.3) * mm});
            skLineSegment(sketch, "E248", {"start": v(173.32, 55.3) * mm, "end": v(176.38, 51.7) * mm});
            skLineSegment(sketch, "E249", {"start": v(176.38, 51.7) * mm, "end": v(180.8, 52.96) * mm});
            skLineSegment(sketch, "E250", {"start": v(180.8, 52.96) * mm, "end": v(178.4, 49.3) * mm});
            skLineSegment(sketch, "E251", {"start": v(178.4, 49.3) * mm, "end": v(180.85, 45.33) * mm});
            skLineSegment(sketch, "E252", {"start": v(180.85, 45.33) * mm, "end": v(176.38, 46.42) * mm});
            skLineSegment(sketch, "E253", {"start": v(176.38, 46.42) * mm, "end": v(173.54, 43.1) * mm});
            skLineSegment(sketch, "E254", {"start": v(173.54, 43.1) * mm, "end": v(173.54, 47.56) * mm});
            skLineSegment(sketch, "E255", {"start": v(173.54, 47.56) * mm, "end": v(169.18, 49.09) * mm});
            skLineSegment(sketch, "E256", {"start": v(169.18, 49.09) * mm, "end": v(173.32, 51) * mm});
            skLineSegment(sketch, "E257", {"start": v(172.07, 36.6) * mm, "end": v(172.07, 37.48) * mm});
            skLineSegment(sketch, "E258", {"start": v(172.07, 37.48) * mm, "end": v(177.74, 39.88) * mm});
            skLineSegment(sketch, "E259", {"start": v(177.74, 39.88) * mm, "end": v(178.12, 21.4) * mm});
            skLineSegment(sketch, "E260", {"start": v(174.3, 34.32) * mm, "end": v(174.3, 21.5) * mm});
            skArc(sketch, "E261", {"start": v(174.3, 34.32) * mm, "mid": v(173.65, 35.92) * mm, "end": v(172.07, 36.6) * mm});
            skArc(sketch, "E262", {"start": v(171.58, 19.33) * mm, "mid": v(173.47, 19.76) * mm, "end": v(174.3, 21.5) * mm});
            skArc(sketch, "E263", {"start": v(178.12, 21.4) * mm, "mid": v(179.13, 19.55) * mm, "end": v(181.23, 19.33) * mm});
            skArc(sketch, "E264", {"start": v(181.23, 19.33) * mm, "mid": v(183.06, 19.79) * mm, "end": v(183.84, 21.5) * mm});
            skArc(sketch, "E265", {"start": v(187.55, 21.4) * mm, "mid": v(188.4, 19.75) * mm, "end": v(190.22, 19.33) * mm});
            skArc(sketch, "E266", {"start": v(183.84, 34.86) * mm, "mid": v(182.88, 36.25) * mm, "end": v(181.23, 36.6) * mm});
            skArc(sketch, "E267", {"start": v(190.06, 36.06) * mm, "mid": v(188.55, 34.76) * mm, "end": v(187.44, 33.12) * mm});
            skArc(sketch, "E268", {"start": v(192.02, 36.06) * mm, "mid": v(191.04, 36.28) * mm, "end": v(190.06, 36.06) * mm});
            skArc(sketch, "E269", {"start": v(192.02, 36.06) * mm, "mid": v(193.84, 35.11) * mm, "end": v(195.67, 36.06) * mm});
            skArc(sketch, "E270", {"start": v(195.67, 36.06) * mm, "mid": v(196.07, 37.93) * mm, "end": v(194.96, 39.5) * mm});
            skArc(sketch, "E271", {"start": v(194.96, 39.5) * mm, "mid": v(192.14, 39.9) * mm, "end": v(189.95, 38.08) * mm});
            skArc(sketch, "E272", {"start": v(189.95, 38.08) * mm, "mid": v(188.54, 36.52) * mm, "end": v(187.39, 34.76) * mm});
            skPoint(sketch, "E272.endSnap0", {"position": v(188.55, 34.76) * mm});
            skLineSegment(sketch, "E273", {"start": v(187.39, 34.76) * mm, "end": v(187.39, 40.04) * mm});
            skLineSegment(sketch, "E274", {"start": v(187.39, 40.04) * mm, "end": v(181.1, 37.38) * mm});
            skLineSegment(sketch, "E275", {"start": v(181.1, 37.38) * mm, "end": v(181.23, 36.6) * mm});
            skLineSegment(sketch, "E276", {"start": v(183.84, 34.86) * mm, "end": v(183.84, 21.5) * mm});
            skLineSegment(sketch, "E277", {"start": v(187.44, 33.12) * mm, "end": v(187.55, 21.4) * mm});
            skLineSegment(sketch, "E278", {"start": v(190.22, 19.33) * mm, "end": v(190.25, 18.07) * mm});
            skLineSegment(sketch, "E279", {"start": v(190.25, 18.07) * mm, "end": v(171.47, 18.07) * mm});
            skLineSegment(sketch, "E280", {"start": v(171.47, 18.07) * mm, "end": v(171.58, 19.33) * mm});
            skLineSegment(sketch, "E281", {"start": v(194.69, 48.87) * mm, "end": v(194.69, 47.61) * mm});
            skLineSegment(sketch, "E282", {"start": v(194.69, 48.87) * mm, "end": v(201.72, 50.94) * mm});
            skLineSegment(sketch, "E283", {"start": v(201.72, 50.94) * mm, "end": v(201.72, 20.8) * mm});
            skLineSegment(sketch, "E284", {"start": v(198.23, 45.27) * mm, "end": v(198.23, 22.05) * mm});
            skLineSegment(sketch, "E285", {"start": v(195.34, 19.22) * mm, "end": v(195.34, 18.08) * mm});
            skLineSegment(sketch, "E286", {"start": v(195.34, 18.08) * mm, "end": v(204.66, 18.08) * mm});
            skLineSegment(sketch, "E287", {"start": v(204.66, 18.08) * mm, "end": v(204.77, 19.17) * mm});
            skArc(sketch, "E288", {"start": v(195.34, 19.22) * mm, "mid": v(197.38, 20.03) * mm, "end": v(198.23, 22.05) * mm});
            skArc(sketch, "E289", {"start": v(201.72, 20.8) * mm, "mid": v(203, 19.54) * mm, "end": v(204.77, 19.17) * mm});
            skArc(sketch, "E290", {"start": v(198.23, 45.27) * mm, "mid": v(197.09, 47.4) * mm, "end": v(194.69, 47.61) * mm});
            skLineSegment(sketch, "E291", {"start": v(207.5, 49.15) * mm, "end": v(207.5, 45) * mm});
            skLineSegment(sketch, "E292", {"start": v(207.5, 45) * mm, "end": v(208.48, 45) * mm});
            skLineSegment(sketch, "E293", {"start": v(208.48, 45) * mm, "end": v(208.48, 46.53) * mm});
            skLineSegment(sketch, "E294", {"start": v(208.48, 46.53) * mm, "end": v(208.94, 46.55) * mm});
            skLineSegment(sketch, "E295", {"start": v(208.94, 46.55) * mm, "end": v(209.98, 45.05) * mm});
            skLineSegment(sketch, "E296", {"start": v(209.98, 45.05) * mm, "end": v(210.67, 45.52) * mm});
            skLineSegment(sketch, "E297", {"start": v(210.67, 45.52) * mm, "end": v(209.8, 46.78) * mm});
            skLineSegment(sketch, "E298", {"start": v(207.5, 49.15) * mm, "end": v(209.11, 49.15) * mm});
            skLineSegment(sketch, "E299", {"start": v(208.48, 48.48) * mm, "end": v(208.48, 47.42) * mm});
            skArc(sketch, "E300", {"start": v(208.48, 47.42) * mm, "mid": v(209.56, 47.95) * mm, "end": v(208.48, 48.48) * mm});
            skArc(sketch, "E301", {"start": v(209.8, 46.78) * mm, "mid": v(210.35, 48.22) * mm, "end": v(209.11, 49.15) * mm});
            skArc(sketch, "E302", {"start": v(208.17, 50.63) * mm, "mid": v(206.28, 49.59) * mm, "end": v(205.38, 47.63) * mm});
            skArc(sketch, "E303", {"start": v(205.38, 47.63) * mm, "mid": v(205.94, 45.14) * mm, "end": v(208.04, 43.68) * mm});
            skArc(sketch, "E304", {"start": v(208.04, 43.68) * mm, "mid": v(210.47, 43.84) * mm, "end": v(212.18, 45.58) * mm});
            skArc(sketch, "E305", {"start": v(212.18, 45.58) * mm, "mid": v(212.47, 47.72) * mm, "end": v(211.43, 49.61) * mm});
            skArc(sketch, "E306", {"start": v(211.43, 49.61) * mm, "mid": v(209.94, 50.58) * mm, "end": v(208.17, 50.63) * mm});
            skArc(sketch, "E307", {"start": v(210.56, 49.34) * mm, "mid": v(209.22, 49.89) * mm, "end": v(207.8, 49.61) * mm});
            skArc(sketch, "E308", {"start": v(211.66, 46.82) * mm, "mid": v(211.48, 48.24) * mm, "end": v(210.56, 49.34) * mm});
            skArc(sketch, "E309", {"start": v(207.8, 49.61) * mm, "mid": v(206.54, 48.59) * mm, "end": v(206.17, 47.01) * mm});
            skArc(sketch, "E310", {"start": v(206.17, 47.01) * mm, "mid": v(207.07, 45) * mm, "end": v(209.2, 44.4) * mm});
            skArc(sketch, "E311", {"start": v(209.2, 44.4) * mm, "mid": v(210.87, 45.15) * mm, "end": v(211.66, 46.82) * mm});
            skSolve(sketch);
        }
        {
            var Q0;
            Q0=makeQuery(id+"F0.imprint","IMPRINT",FACE,{"disambiguationData":[TD([[makeQuery(id+"F0.imprint","IMPRINT",EDGE,{"derivedFrom":sQuery(id+"F0.wireOp",EDGE,"E0")}),-1.0]])]});
            var Q1;
            Q1=makeQuery(id+"F0.imprint","IMPRINT",FACE,{"disambiguationData":[TD([[makeQuery(id+"F0.imprint","IMPRINT",EDGE,{"derivedFrom":sQuery(id+"F0.wireOp",EDGE,"E20")}),-1.0]])]});
            var Q2;
            Q2=makeQuery(id+"F0.imprint","IMPRINT",FACE,{"disambiguationData":[TD([[makeQuery(id+"F0.imprint","IMPRINT",EDGE,{"derivedFrom":sQuery(id+"F0.wireOp",EDGE,"E93")}),-1.0]])]});
            var Q3;
            Q3=makeQuery(id+"F0.imprint","IMPRINT",FACE,{"disambiguationData":[TD([[makeQuery(id+"F0.imprint","IMPRINT",EDGE,{"derivedFrom":sQuery(id+"F0.wireOp",EDGE,"E113")}),1.0]])]});
            var Q4;
            Q4=makeQuery(id+"F0.imprint","IMPRINT",FACE,{"disambiguationData":[TD([[makeQuery(id+"F0.imprint","IMPRINT",EDGE,{"derivedFrom":sQuery(id+"F0.wireOp",EDGE,"E133")}),1.0]])]});
            var Q5;
            Q5=makeQuery(id+"F0.imprint","IMPRINT",FACE,{"disambiguationData":[TD([[makeQuery(id+"F0.imprint","IMPRINT",EDGE,{"derivedFrom":sQuery(id+"F0.wireOp",EDGE,"E136")}),1.0]])]});
            var Q6;
            Q6=makeQuery(id+"F0.imprint","IMPRINT",FACE,{"disambiguationData":[TD([[makeQuery(id+"F0.imprint","IMPRINT",EDGE,{"derivedFrom":sQuery(id+"F0.wireOp",EDGE,"E155")}),-1.0]])]});
            var Q7;
            Q7=makeQuery(id+"F0.imprint","IMPRINT",FACE,{"disambiguationData":[TD([[makeQuery(id+"F0.imprint","IMPRINT",EDGE,{"derivedFrom":sQuery(id+"F0.wireOp",EDGE,"E173")}),1.0]])]});
            var Q8;
            Q8=makeQuery(id+"F0.imprint","IMPRINT",FACE,{"disambiguationData":[TD([[makeQuery(id+"F0.imprint","IMPRINT",EDGE,{"derivedFrom":sQuery(id+"F0.wireOp",EDGE,"E198")}),1.0]])]});
            extrude(context, id + "F1", {"entities" : qUnion([Q0, Q1, Q2, Q3, Q4, Q5, Q6, Q7, Q8]), "depth" : 76.2 * mm, "offsetDistance" : 25.4 * mm, "symmetric" : true});
        }
        {
            var Q0;
            Q0=makeQuery(id+"F0.imprint","IMPRINT",FACE,{"disambiguationData":[TD([[makeQuery(id+"F0.imprint","IMPRINT",EDGE,{"derivedFrom":sQuery(id+"F0.wireOp",EDGE,"E222")}),-1.0]])]});
            var Q1;
            Q1=makeQuery(id+"F0.imprint","IMPRINT",FACE,{"disambiguationData":[TD([[makeQuery(id+"F0.imprint","IMPRINT",EDGE,{"derivedFrom":sQuery(id+"F0.wireOp",EDGE,"E247")}),-1.0]])]});
            var Q2;
            Q2=makeQuery(id+"F0.imprint","IMPRINT",FACE,{"disambiguationData":[TD([[makeQuery(id+"F0.imprint","IMPRINT",EDGE,{"derivedFrom":sQuery(id+"F0.wireOp",EDGE,"E257")}),-1.0]])]});
            var Q3;
            Q3=makeQuery(id+"F0.imprint","IMPRINT",FACE,{"disambiguationData":[TD([[makeQuery(id+"F0.imprint","IMPRINT",EDGE,{"derivedFrom":sQuery(id+"F0.wireOp",EDGE,"E281")}),1.0]])]});
            extrude(context, id + "F2", {"entities" : qUnion([Q0, Q1, Q2, Q3]), "depth" : 76.2 * mm, "offsetDistance" : 25.4 * mm, "symmetric" : true});
        }
        {
            var Q0;
            Q0=makeQuery(id+"F0.imprint","IMPRINT",FACE,{"disambiguationData":[TD([[makeQuery(id+"F0.imprint","IMPRINT",EDGE,{"derivedFrom":sQuery(id+"F0.wireOp",EDGE,"E291")}),1.0]])]});
            var Q1;
            Q1=makeQuery(id+"F0.imprint","IMPRINT",FACE,{"disambiguationData":[TD([[makeQuery(id+"F0.imprint","IMPRINT",EDGE,{"derivedFrom":sQuery(id+"F0.wireOp",EDGE,"E302")}),1.0]])]});
            extrude(context, id + "F3", {"entities" : qUnion([Q0, Q1]), "depth" : 76.2 * mm, "offsetDistance" : 25.4 * mm, "symmetric" : true});
        }
    });
